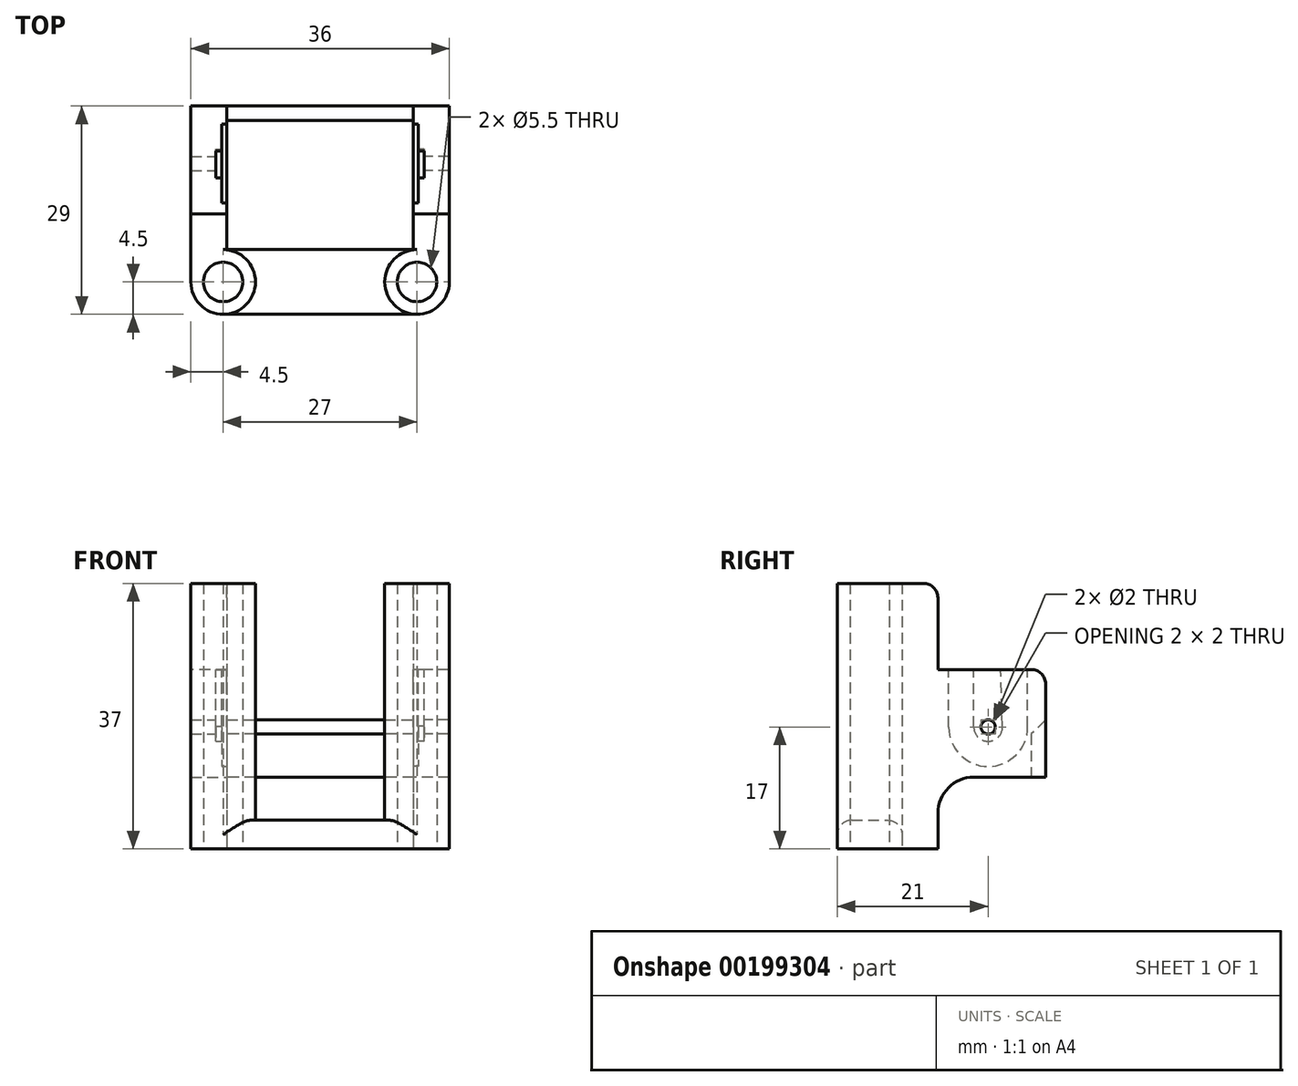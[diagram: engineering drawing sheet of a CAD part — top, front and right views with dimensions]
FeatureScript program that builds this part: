
annotation { "Feature Type Name" : "Feature", "Feature Type Description" : "" }
export const myFeature = defineFeature(function(context is Context, id is Id, definition is map)
    precondition{}
    {
        {
            var Q0;
            Q0=qCreatedBy(makeId("Top.planeOp"),FACE);
            var sketch = newSketch(context, id + "F0", { "sketchPlane" : qUnion([Q0])});
            skLineSegment(sketch, "E0.bottom", {"start": v(0, 0) * mm, "end": v(-18, 0) * mm});
            skLineSegment(sketch, "E0.top", {"start": v(0, -9) * mm, "end": v(-18, -9) * mm});
            skLineSegment(sketch, "E0.left", {"start": v(0, 0) * mm, "end": v(0, -9) * mm});
            skLineSegment(sketch, "E0.right", {"start": v(-18, 0) * mm, "end": v(-18, -9) * mm});
            skPoint(sketch, "E1", {"position": v(-13.5, -4.5) * mm});
            skPoint(sketch, "E1.positionSnap0", {"position": v(-18, -4.5) * mm});
            skCircle(sketch, "E2", {"center": v(-13.5, -4.5) * mm, "radius": 2.75 * mm});
            skCircle(sketch, "E3", {"center": v(-13.5, -4.5) * mm, "radius": 4.5 * mm});
            skLineSegment(sketch, "E4", {"start": v(-18, 0) * mm, "end": v(-18, 5) * mm});
            skLineSegment(sketch, "E5", {"start": v(-18, 5) * mm, "end": v(-13, 5) * mm});
            skLineSegment(sketch, "E6", {"start": v(-13, 5) * mm, "end": v(-13, 0) * mm});
            skLineSegment(sketch, "E7", {"start": v(-13, 5) * mm, "end": v(-13, 20) * mm});
            skLineSegment(sketch, "E8", {"start": v(-13, 20) * mm, "end": v(-18, 20) * mm});
            skLineSegment(sketch, "E9", {"start": v(-18, 20) * mm, "end": v(-18, 5) * mm});
            skLineSegment(sketch, "E10", {"start": v(-13, 20) * mm, "end": v(0, 20) * mm});
            skLineSegment(sketch, "E11", {"start": v(0, 20) * mm, "end": v(0, 18) * mm});
            skLineSegment(sketch, "E12", {"start": v(0, 18) * mm, "end": v(-13, 18) * mm});
            skSolve(sketch);
        }
        {
            var Q0;
            {var subQ0=sQuery(id+"F0.wireOp",EDGE,"E0.left");Q0=makeQuery(id+"F0.imprint","IMPRINT",FACE,{"disambiguationData":[TD([[makeQuery(id+"F0.imprint","IMPRINT",EDGE,{"derivedFrom":subQ0}),-1.0]])]});}
            extrude(context, id + "F1", {"entities" : qUnion([Q0]), "depth" : 4 * mm});
        }
        {
            var Q0;
            Q0=makeQuery(id+"F0.imprint","IMPRINT",FACE,{"disambiguationData":[TD([[makeQuery(id+"F0.imprint","IMPRINT",EDGE,{"derivedFrom":sQuery(id+"F0.wireOp",EDGE,"E2")}),-1.0]])]});
            var Q1;
            {var subQ0=sQuery(id+"F0.wireOp",EDGE,"E4");Q1=makeQuery(id+"F0.imprint","IMPRINT",FACE,{"disambiguationData":[TD([[makeQuery(id+"F0.imprint","IMPRINT",EDGE,{"derivedFrom":subQ0}),-1.0]])]});}
            var Q2;
            {var subQ0=sQuery(id+"F0.wireOp",EDGE,"E0.right");var subQ3=sQuery(id+"F0.wireOp",EDGE,"E3");var subQ5=makeQuery(id+"F0.imprint","INTERSECT",VERTEX,{"derivedFrom":[subQ0,subQ3]});Q2=makeQuery(id+"F0.imprint","IMPRINT",FACE,{"disambiguationData":[TD([[makeQuery(id+"F0.imprint","IMPRINT",EDGE,{"disambiguationData":[TD([[subQ5,1.0]])],"derivedFrom":subQ3}),-1.0]])]});}
            extrude(context, id + "F2", {"entities" : qUnion([Q0, Q1, Q2]), "operationType" : NewBodyOperationType.ADD, "depth" : 37 * mm});
        }
        {
            var Q0;
            {var subQ3=sQuery(id+"F0.wireOp",EDGE,"E5");Q0=makeQuery(id+"F0.imprint","IMPRINT",FACE,{"disambiguationData":[TD([[makeQuery(id+"F0.imprint","IMPRINT",EDGE,{"derivedFrom":subQ3}),1.0]])]});}
            extrude(context, id + "F3", {"entities" : qUnion([Q0]), "operationType" : NewBodyOperationType.ADD, "depth" : 25 * mm});
        }
        {
            var Q0;
            {var subQ0=sQuery(id+"F0.wireOp",EDGE,"E10");Q0=makeQuery(id+"F0.imprint","IMPRINT",FACE,{"disambiguationData":[TD([[makeQuery(id+"F0.imprint","IMPRINT",EDGE,{"derivedFrom":subQ0}),-1.0]])]});}
            extrude(context, id + "F4", {"entities" : qUnion([Q0]), "operationType" : NewBodyOperationType.ADD, "depth" : 18 * mm});
        }
        {
            var Q0;
            Q0=makeQuery(id+"F1.opExtrude","CAP_EDGE",EDGE,{"disambiguationData":[OSD([sQuery(id+"F0.wireOp",EDGE,"E0.top")])],"isStart":false});
            var Q1;
            {var subQ0=sQuery(id+"F0.wireOp",EDGE,"E0.bottom");var subQ1=sQuery(id+"F0.wireOp",EDGE,"E0.left");Q1=makeQuery(id+"F2.boolean.opBoolean","SPLIT",EDGE,{"disambiguationData":[TD([makeQuery(id+"F1.opExtrude","SWEPT_FACE",FACE,{"disambiguationData":[OSD([subQ1])]})])],"derivedFrom":makeQuery(id+"F1.opExtrude","CAP_EDGE",EDGE,{"disambiguationData":[OSD([subQ0])],"isStart":false})});}
            var Q2;
            Q2=makeQuery(id+"F2.opExtrude","CAP_EDGE",EDGE,{"disambiguationData":[OSD([sQuery(id+"F0.wireOp",EDGE,"E5")])],"isStart":false});
            var Q3;
            Q3=makeQuery(id+"F3.opExtrude","CAP_EDGE",EDGE,{"disambiguationData":[OSD([sQuery(id+"F0.wireOp",EDGE,"E8")])],"isStart":false});
            fillet(context, id + "F5", {"entities" : qUnion([Q0, Q1, Q2, Q3]), "radius" : 2 * mm, "tangentPropagation" : true, "allowEdgeOverflow" : false});
        }
        {
            var Q0;
            {var subQ3=sQuery(id+"F0.wireOp",EDGE,"E5");Q0=makeQuery(id+"F0.imprint","IMPRINT",FACE,{"disambiguationData":[TD([[makeQuery(id+"F0.imprint","IMPRINT",EDGE,{"derivedFrom":subQ3}),1.0]])]});}
            var Q1;
            {var subQ0=sQuery(id+"F0.wireOp",EDGE,"E10");Q1=makeQuery(id+"F0.imprint","IMPRINT",FACE,{"disambiguationData":[TD([[makeQuery(id+"F0.imprint","IMPRINT",EDGE,{"derivedFrom":subQ0}),-1.0]])]});}
            extrude(context, id + "F6", {"entities" : qUnion([Q0, Q1]), "operationType" : NewBodyOperationType.REMOVE, "depth" : 10 * mm});
        }
        {
            var Q0;
            Q0=makeQuery(id+"F3.boolean.opBoolean","MERGE",FACE,{"derivedFrom":[makeQuery(id+"F2.opExtrude","SWEPT_FACE",FACE,{"disambiguationData":[OSD([sQuery(id+"F0.wireOp",EDGE,"E6")])]}),makeQuery(id+"F3.opExtrude","SWEPT_FACE",FACE,{"disambiguationData":[OSD([sQuery(id+"F0.wireOp",EDGE,"E7")])]})]});
            var sketch = newSketch(context, id + "F7", { "sketchPlane" : qUnion([Q0])});
            skPoint(sketch, "E13", {"position": v(12, 17) * mm});
            skCircle(sketch, "E14", {"center": v(12, 17) * mm, "radius": 5.5 * mm});
            skLineSegment(sketch, "E15", {"start": v(6.5, 17) * mm, "end": v(6.5, 25) * mm});
            skLineSegment(sketch, "E16", {"start": v(17.5, 17) * mm, "end": v(17.5, 25) * mm});
            skSolve(sketch);
        }
        {
            var Q0;
            Q0=sQuery(id+"F7.wireOp",VERTEX,"E13");
            var Q1;
            Q1=makeQuery(id+"F1.opExtrude","SWEPT_BODY",BODY,{"disambiguationData":[OSD([sQuery(id+"F0.wireOp",EDGE,"E0.bottom"),sQuery(id+"F0.wireOp",EDGE,"E0.top"),sQuery(id+"F0.wireOp",EDGE,"E0.left"),sQuery(id+"F0.wireOp",EDGE,"E3")])]});
            hole(context, id + "F8", {"style" : HoleStyle.C_BORE, "endStyle" : HoleEndStyle.THROUGH, "holeDiameter" : 2 * mm, "cBoreDiameter" : 4 * mm, "cBoreDepth" : 1.5 * mm, "locations" : qUnion([Q0]), "scope" : qUnion([Q1]), "isTappedThrough" : true});
        }
        {
            var Q0;
            {var subQ0=sQuery(id+"F7.wireOp",EDGE,"E14");var subQ1=makeQuery(id+"F7.imprint","INTERSECT",VERTEX,{"derivedFrom":[subQ0,sQuery(id+"F7.wireOp",EDGE,"E15")]});Q0=makeQuery(id+"F7.imprint","IMPRINT",FACE,{"disambiguationData":[TD([[makeQuery(id+"F7.imprint","IMPRINT",EDGE,{"disambiguationData":[TD([[subQ1,1.0]])],"derivedFrom":subQ0}),1.0]])]});}
            var Q1;
            {var subQ0=sQuery(id+"F7.wireOp",EDGE,"E15");Q1=makeQuery(id+"F7.imprint","IMPRINT",FACE,{"disambiguationData":[TD([[makeQuery(id+"F7.imprint","IMPRINT",EDGE,{"derivedFrom":subQ0}),-1.0]])]});}
            var Q2;
            {var subQ0=sQuery(id+"F7.wireOp",EDGE,"E16");Q2=makeQuery(id+"F7.imprint","IMPRINT",FACE,{"disambiguationData":[TD([[makeQuery(id+"F7.imprint","IMPRINT",EDGE,{"derivedFrom":subQ0}),1.0]])]});}
            extrude(context, id + "F9", {"entities" : qUnion([Q0, Q1, Q2]), "operationType" : NewBodyOperationType.REMOVE, "oppositeDirection" : true, "depth" : 0.7 * mm});
        }
        {
            var Q0;
            Q0=makeQuery(id+"F6.boolean.opBoolean","COPY",EDGE,{"derivedFrom":makeQuery(id+"F6.opExtrude","CAP_EDGE",EDGE,{"disambiguationData":[OSD([sQuery(id+"F0.wireOp",EDGE,"E5")])],"isStart":false})});
            var Q1;
            Q1=makeQuery(id+"F3.opExtrude","CAP_EDGE",EDGE,{"disambiguationData":[OSD([sQuery(id+"F0.wireOp",EDGE,"E5")])],"isStart":false});
            fillet(context, id + "F10", {"entities" : qUnion([Q0, Q1]), "radius" : 5 * mm, "tangentPropagation" : true, "allowEdgeOverflow" : false});
        }
        {
            var Q0;
            {var subQ0=makeQuery(id+"F4.opExtrude","CAP_EDGE",EDGE,{"disambiguationData":[OSD([sQuery(id+"F0.wireOp",EDGE,"E12")])],"isStart":false});Q0=makeQuery(id+"F14.boolean.opBoolean","MERGE",EDGE,{"derivedFrom":[subQ0,makeQuery(id+"F14.opPattern","COPY",EDGE,{"derivedFrom":subQ0,"instanceName":"1"})]});}
            chamfer(context, id + "F11", {"entities" : qUnion([Q0]), "width" : 2 * mm, "tangentPropagation" : true});
        }
        {
            var Q0;
            Q0=makeQuery(id+"F9.boolean.opBoolean","COPY",FACE,{"derivedFrom":makeQuery(id+"F9.opExtrude","CAP_FACE",FACE,{"disambiguationData":[OSD([sQuery(id+"F0.wireOp",EDGE,"E7"),sQuery(id+"F7.wireOp",EDGE,"E14"),sQuery(id+"F7.wireOp",EDGE,"E15"),sQuery(id+"F7.wireOp",EDGE,"E16")])],"isStart":false})});
            var sketch = newSketch(context, id + "F12", { "sketchPlane" : qUnion([Q0])});
            skPoint(sketch, "E17", {"position": v(12, 17) * mm});
            skLineSegment(sketch, "E18", {"start": v(10, 17) * mm, "end": v(10, 25) * mm});
            skLineSegment(sketch, "E19", {"start": v(14, 17) * mm, "end": v(13.75, 25) * mm});
            skSolve(sketch);
        }
        {
            var Q0;
            {var subQ0=sQuery(id+"F12.wireOp",EDGE,"E18");Q0=makeQuery(id+"F12.imprint","IMPRINT",FACE,{"disambiguationData":[TD([[makeQuery(id+"F12.imprint","IMPRINT",EDGE,{"derivedFrom":subQ0}),-1.0]])]});}
            extrude(context, id + "F13", {"entities" : qUnion([Q0]), "operationType" : NewBodyOperationType.REMOVE, "oppositeDirection" : true, "depth" : 0.8 * mm});
        }
        {
            var Q0;
            Q0=makeQuery(id+"F1.opExtrude","SWEPT_BODY",BODY,{"disambiguationData":[OSD([sQuery(id+"F0.wireOp",EDGE,"E0.bottom"),sQuery(id+"F0.wireOp",EDGE,"E0.top"),sQuery(id+"F0.wireOp",EDGE,"E0.left"),sQuery(id+"F0.wireOp",EDGE,"E3")])]});
            var Q1;
            Q1=makeQuery(id+"F4.opExtrude","SWEPT_FACE",FACE,{"disambiguationData":[OSD([sQuery(id+"F0.wireOp",EDGE,"E11")])]});
            mirror(context, id + "F14", {"operationType" : NewBodyOperationType.ADD, "entities" : qUnion([Q0]), "mirrorPlane" : qUnion([Q1])});
        }
    });
